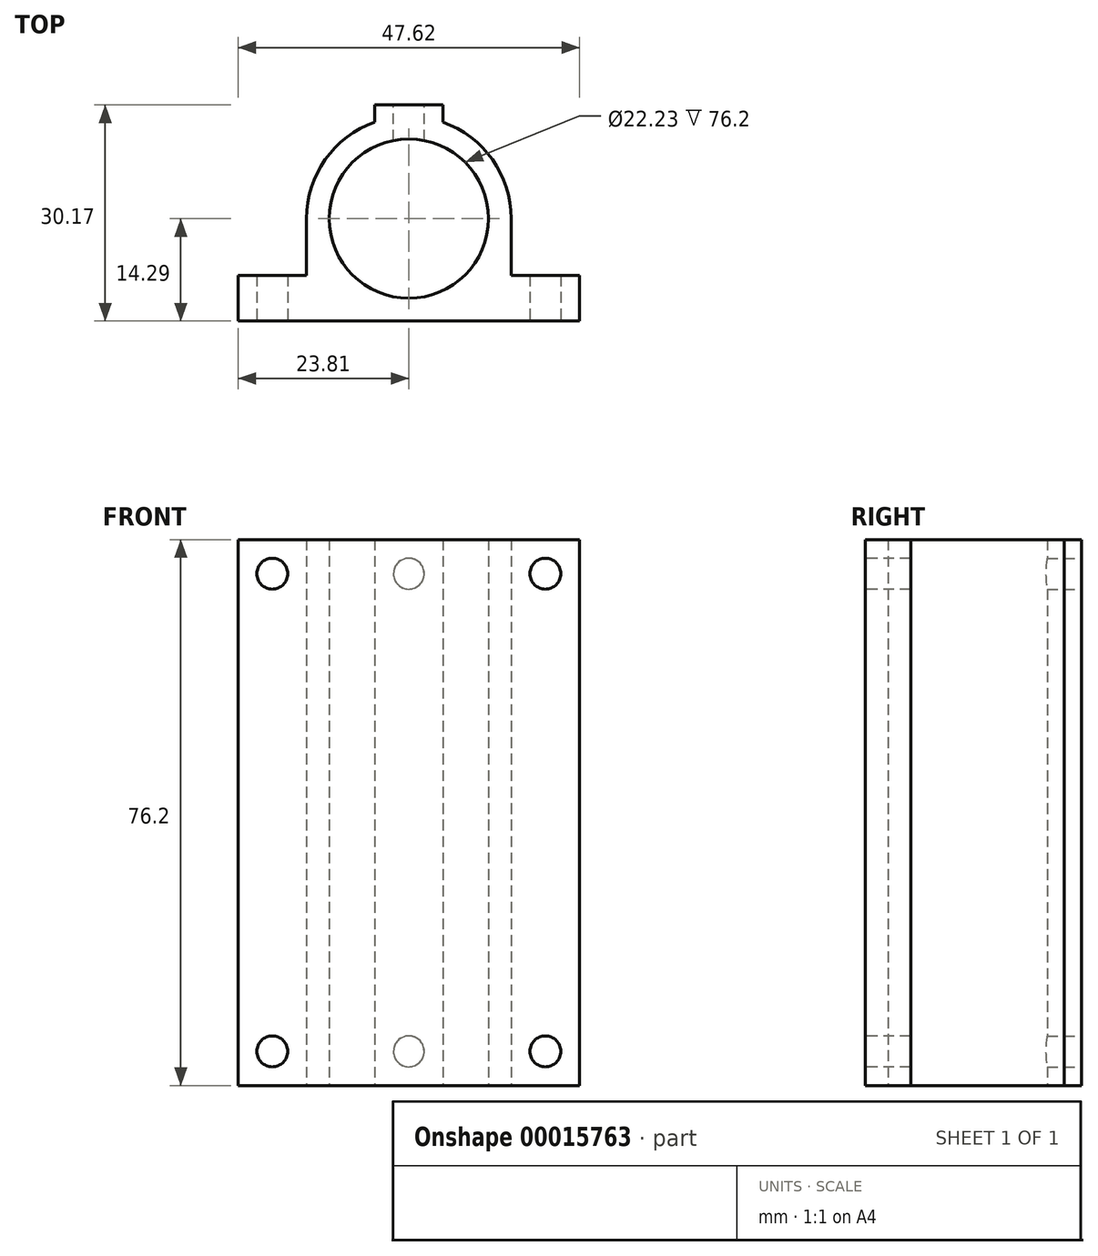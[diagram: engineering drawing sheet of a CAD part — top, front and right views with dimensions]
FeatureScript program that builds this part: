
annotation { "Feature Type Name" : "Feature", "Feature Type Description" : "" }
export const myFeature = defineFeature(function(context is Context, id is Id, definition is map)
    precondition{}
    {
        {
            var Q0;
            Q0=qCreatedBy(makeId("Top.planeOp"),FACE);
            var sketch = newSketch(context, id + "F0", { "sketchPlane" : qUnion([Q0])});
            skCircle(sketch, "E0", {"center": v(0, 0) * mm, "radius": 11.11 * mm});
            skLineSegment(sketch, "E1", {"start": v(0, 0) * mm, "end": v(0, 13.47) * mm, "construction": true});
            skLineSegment(sketch, "E2", {"start": v(-4.76, 13.47) * mm, "end": v(4.76, 13.47) * mm, "construction": true});
            skArc(sketch, "E3", {"start": v(-4.76, 13.47) * mm, "mid": v(-11.67, 8.25) * mm, "end": v(-14.29, 0) * mm});
            skArc(sketch, "E4", {"start": v(14.29, 0) * mm, "mid": v(11.67, 8.25) * mm, "end": v(4.76, 13.47) * mm});
            skLineSegment(sketch, "E5.top", {"start": v(-4.76, 15.88) * mm, "end": v(4.76, 15.88) * mm});
            skLineSegment(sketch, "E5.left", {"start": v(-4.76, 13.47) * mm, "end": v(-4.76, 15.88) * mm});
            skLineSegment(sketch, "E5.right", {"start": v(4.76, 13.47) * mm, "end": v(4.76, 15.88) * mm});
            skLineSegment(sketch, "E6.bottom", {"start": v(23.81, -14.29) * mm, "end": v(-23.81, -14.29) * mm});
            skLineSegment(sketch, "E6.left", {"start": v(23.81, -14.29) * mm, "end": v(23.81, -7.94) * mm});
            skLineSegment(sketch, "E6.right", {"start": v(-23.81, -14.29) * mm, "end": v(-23.81, -7.94) * mm});
            skLineSegment(sketch, "E7.bottom", {"start": v(14.29, 0) * mm, "end": v(-14.29, 0) * mm, "construction": true});
            skLineSegment(sketch, "E7.left", {"start": v(14.29, 0) * mm, "end": v(14.29, -7.94) * mm});
            skLineSegment(sketch, "E7.right", {"start": v(-14.29, 0) * mm, "end": v(-14.29, -7.94) * mm});
            skLineSegment(sketch, "E8", {"start": v(-23.81, -7.94) * mm, "end": v(-14.29, -7.94) * mm});
            skLineSegment(sketch, "E9", {"start": v(14.29, -7.94) * mm, "end": v(23.81, -7.94) * mm});
            skLineSegment(sketch, "E10", {"start": v(0, 0) * mm, "end": v(0, -14.29) * mm, "construction": true});
            skSolve(sketch);
        }
        {
            var Q0;
            Q0=qSketchRegion(id+"F0",true);
            extrude(context, id + "F1", {"entities" : qUnion([Q0]), "depth" : 76.2 * mm});
        }
        {
            var Q0;
            Q0=makeQuery(id+"F1.opExtrude","SWEPT_FACE",FACE,{"disambiguationData":[OSD([sQuery(id+"F0.wireOp",EDGE,"E5.top")])]});
            var sketch = newSketch(context, id + "F2", { "sketchPlane" : qUnion([Q0])});
            skLineSegment(sketch, "E11.bottom", {"start": v(0, 0) * mm, "end": v(4.76, 0) * mm, "construction": true});
            skLineSegment(sketch, "E11.top", {"start": v(0, 4.76) * mm, "end": v(4.76, 4.76) * mm, "construction": true});
            skLineSegment(sketch, "E11.left", {"start": v(0, 0) * mm, "end": v(0, 4.76) * mm, "construction": true});
            skLineSegment(sketch, "E11.right", {"start": v(4.76, 0) * mm, "end": v(4.76, 4.76) * mm, "construction": true});
            skLineSegment(sketch, "E12.left", {"start": v(0, 4.76) * mm, "end": v(0, 71.44) * mm, "construction": true});
            skCircle(sketch, "E13", {"center": v(0, 4.76) * mm, "radius": 2.15 * mm});
            skCircle(sketch, "E14", {"center": v(0, 71.44) * mm, "radius": 2.15 * mm});
            skLineSegment(sketch, "E15.bottom", {"start": v(0, 71.44) * mm, "end": v(-4.76, 71.44) * mm, "construction": true});
            skLineSegment(sketch, "E15.top", {"start": v(0, 76.2) * mm, "end": v(-4.76, 76.2) * mm, "construction": true});
            skLineSegment(sketch, "E15.left", {"start": v(0, 71.44) * mm, "end": v(0, 76.2) * mm, "construction": true});
            skLineSegment(sketch, "E15.right", {"start": v(-4.76, 71.44) * mm, "end": v(-4.76, 76.2) * mm, "construction": true});
            skSolve(sketch);
        }
        {
            var Q0;
            Q0=qSketchRegion(id+"F2",true);
            var Q1;
            Q1=makeQuery(id+"F1.opExtrude","SWEPT_FACE",FACE,{"disambiguationData":[OSD([sQuery(id+"F0.wireOp",EDGE,"djldysEu-ljvw-hPGd-3HMA-uMFqrL7TPg54")])]});
            extrude(context, id + "F3", {"entities" : qUnion([Q0]), "operationType" : NewBodyOperationType.REMOVE, "oppositeDirection" : true, "endBoundEntityFace" : qUnion([Q1]), "depth" : 6.35 * mm});
        }
        {
            var Q0;
            Q0=makeQuery(id+"F1.opExtrude","SWEPT_FACE",FACE,{"disambiguationData":[OSD([sQuery(id+"F0.wireOp",EDGE,"E6.bottom")])]});
            var sketch = newSketch(context, id + "F4", { "sketchPlane" : qUnion([Q0])});
            skLineSegment(sketch, "E16", {"start": v(0, 76.2) * mm, "end": v(0, 0) * mm, "construction": true});
            skLineSegment(sketch, "E17.bottom", {"start": v(-23.81, 76.2) * mm, "end": v(-19.05, 76.2) * mm, "construction": true});
            skLineSegment(sketch, "E17.top", {"start": v(-23.81, 71.44) * mm, "end": v(-19.05, 71.44) * mm, "construction": true});
            skLineSegment(sketch, "E17.left", {"start": v(-23.81, 76.2) * mm, "end": v(-23.81, 71.44) * mm, "construction": true});
            skLineSegment(sketch, "E17.right", {"start": v(-19.05, 76.2) * mm, "end": v(-19.05, 71.44) * mm, "construction": true});
            skLineSegment(sketch, "E18.bottom", {"start": v(-19.05, 71.44) * mm, "end": v(19.05, 71.44) * mm, "construction": true});
            skLineSegment(sketch, "E18.top", {"start": v(-19.05, 4.76) * mm, "end": v(19.05, 4.76) * mm, "construction": true});
            skLineSegment(sketch, "E18.left", {"start": v(-19.05, 71.44) * mm, "end": v(-19.05, 4.76) * mm, "construction": true});
            skLineSegment(sketch, "E18.right", {"start": v(19.05, 71.44) * mm, "end": v(19.05, 4.76) * mm, "construction": true});
            skPoint(sketch, "E18.middle", {"position": v(0, 38.1) * mm});
            skCircle(sketch, "E19", {"center": v(-19.05, 71.44) * mm, "radius": 2.15 * mm});
            skCircle(sketch, "E20", {"center": v(19.05, 71.44) * mm, "radius": 2.15 * mm});
            skCircle(sketch, "E21", {"center": v(19.05, 4.76) * mm, "radius": 2.15 * mm});
            skCircle(sketch, "E22", {"center": v(-19.05, 4.76) * mm, "radius": 2.15 * mm});
            skSolve(sketch);
        }
        {
            var Q0;
            Q0=qSketchRegion(id+"F4",true);
            var Q1;
            Q1=makeQuery(id+"F1.opExtrude","SWEPT_FACE",FACE,{"disambiguationData":[OSD([sQuery(id+"F0.wireOp",EDGE,"E9")])]});
            extrude(context, id + "F5", {"entities" : qUnion([Q0]), "operationType" : NewBodyOperationType.REMOVE, "endBound" : BoundingType.UP_TO_SURFACE, "oppositeDirection" : true, "endBoundEntityFace" : qUnion([Q1]), "depth" : 25.4 * mm});
        }
    });
